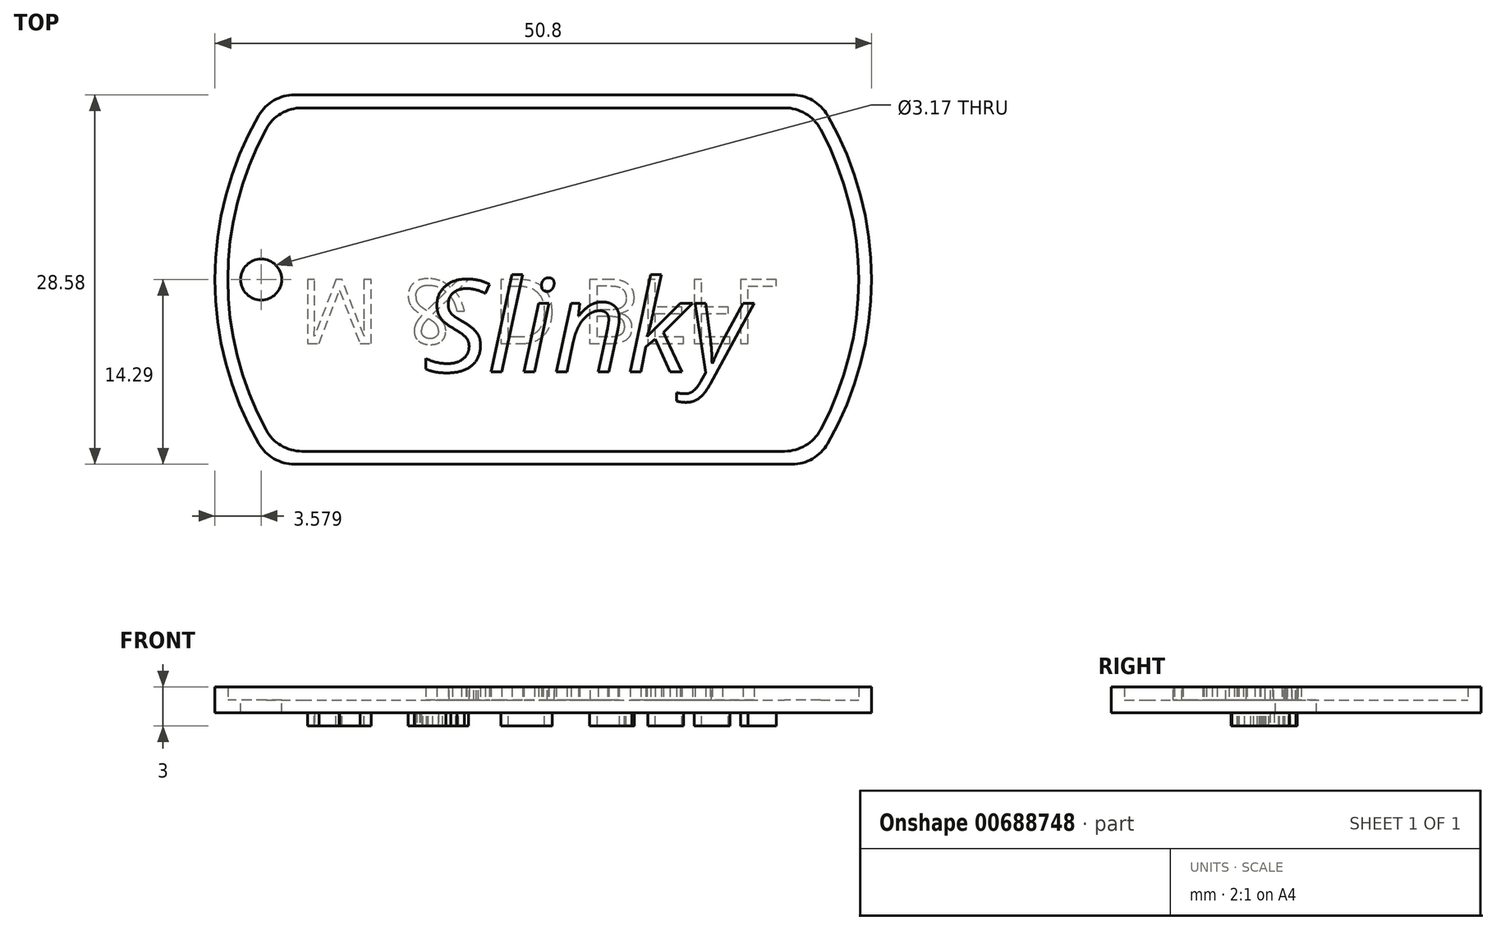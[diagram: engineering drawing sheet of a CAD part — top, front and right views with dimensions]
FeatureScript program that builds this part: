
annotation { "Feature Type Name" : "Feature", "Feature Type Description" : "" }
export const myFeature = defineFeature(function(context is Context, id is Id, definition is map)
    precondition{}
    {
        {
            var Q0;
            Q0=qCreatedBy(makeId("Top.planeOp"),FACE);
            var sketch = newSketch(context, id + "F0", { "sketchPlane" : qUnion([Q0])});
            skArc(sketch, "E0", {"start": v(-22, 12.7) * mm, "mid": v(-25.4, 0) * mm, "end": v(-22, -12.7) * mm});
            skLineSegment(sketch, "E1.top", {"start": v(-19.25, -14.29) * mm, "end": v(19.25, -14.29) * mm});
            skArc(sketch, "E2.trimOffspring", {"start": v(22, -12.7) * mm, "mid": v(25.4, 0) * mm, "end": v(22, 12.7) * mm});
            skLineSegment(sketch, "E3", {"start": v(-19.25, 14.29) * mm, "end": v(19.25, 14.29) * mm});
            skPoint(sketch, "E4.visualSharp", {"position": v(-21, 14.29) * mm});
            skArc(sketch, "E4.filletArc", {"start": v(-19.25, 14.29) * mm, "mid": v(-20.83, 13.86) * mm, "end": v(-22, 12.7) * mm});
            skPoint(sketch, "E5.visualSharp", {"position": v(21, 14.29) * mm});
            skArc(sketch, "E5.filletArc", {"start": v(22, 12.7) * mm, "mid": v(20.83, 13.86) * mm, "end": v(19.25, 14.29) * mm});
            skPoint(sketch, "E6.visualSharp", {"position": v(21, -14.29) * mm});
            skArc(sketch, "E6.filletArc", {"start": v(19.25, -14.29) * mm, "mid": v(20.83, -13.86) * mm, "end": v(22, -12.7) * mm});
            skPoint(sketch, "E7.visualSharp", {"position": v(-21, -14.29) * mm});
            skArc(sketch, "E7.filletArc", {"start": v(-22, -12.7) * mm, "mid": v(-20.83, -13.86) * mm, "end": v(-19.25, -14.29) * mm});
            skSolve(sketch);
        }
        {
            var Q0;
            Q0=makeQuery(id+"F0.imprint","IMPRINT",FACE,{"disambiguationData":[TD([[makeQuery(id+"F0.imprint","IMPRINT",EDGE,{"derivedFrom":sQuery(id+"F0.wireOp",EDGE,"E0")}),1.0]])]});
            extrude(context, id + "F1", {"entities" : qUnion([Q0]), "depth" : 1 * mm, "offsetDistance" : 25.4 * mm});
        }
        {
            var Q0;
            Q0=makeQuery(id+"F1.opExtrude","CAP_FACE",FACE,{"disambiguationData":[OSD([sQuery(id+"F0.wireOp",EDGE,"E0"),sQuery(id+"F0.wireOp",EDGE,"E1.top"),sQuery(id+"F0.wireOp",EDGE,"E2.trimOffspring"),sQuery(id+"F0.wireOp",EDGE,"E3"),sQuery(id+"F0.wireOp",EDGE,"E4.filletArc"),sQuery(id+"F0.wireOp",EDGE,"E5.filletArc"),sQuery(id+"F0.wireOp",EDGE,"E6.filletArc"),sQuery(id+"F0.wireOp",EDGE,"E7.filletArc")])],"isStart":false});
            var sketch = newSketch(context, id + "F2", { "sketchPlane" : qUnion([Q0])});
            skLineSegment(sketch, "E8.0", {"start": v(-18.66, 13.29) * mm, "end": v(18.66, 13.29) * mm});
            skArc(sketch, "E8.1", {"start": v(-21.45, 11.63) * mm, "mid": v(-24.4, 0) * mm, "end": v(-21.45, -11.63) * mm});
            skLineSegment(sketch, "E8.2", {"start": v(-18.66, -13.29) * mm, "end": v(18.66, -13.29) * mm});
            skArc(sketch, "E8.3", {"start": v(21.45, -11.63) * mm, "mid": v(24.4, 0) * mm, "end": v(21.45, 11.63) * mm});
            skPoint(sketch, "E9.visualSharp", {"position": v(-20.46, 13.29) * mm});
            skArc(sketch, "E9.filletArc", {"start": v(-18.66, 13.29) * mm, "mid": v(-20.29, 12.84) * mm, "end": v(-21.45, 11.63) * mm});
            skPoint(sketch, "E10.visualSharp", {"position": v(20.46, 13.29) * mm});
            skArc(sketch, "E10.filletArc", {"start": v(21.45, 11.63) * mm, "mid": v(20.29, 12.84) * mm, "end": v(18.66, 13.29) * mm});
            skPoint(sketch, "E11.visualSharp", {"position": v(20.46, -13.29) * mm});
            skArc(sketch, "E11.filletArc", {"start": v(18.66, -13.29) * mm, "mid": v(20.29, -12.84) * mm, "end": v(21.45, -11.63) * mm});
            skPoint(sketch, "E12.visualSharp", {"position": v(-20.46, -13.29) * mm});
            skArc(sketch, "E12.filletArc", {"start": v(-21.45, -11.63) * mm, "mid": v(-20.29, -12.84) * mm, "end": v(-18.66, -13.29) * mm});
            skLineSegment(sketch, "E13.0", {"start": v(-19.25, 14.29) * mm, "end": v(19.25, 14.29) * mm});
            skArc(sketch, "E13.1", {"start": v(-22, 12.7) * mm, "mid": v(-25.4, 0) * mm, "end": v(-22, -12.7) * mm});
            skLineSegment(sketch, "E13.2", {"start": v(-19.25, -14.29) * mm, "end": v(19.25, -14.29) * mm});
            skArc(sketch, "E13.3", {"start": v(22, -12.7) * mm, "mid": v(25.4, 0) * mm, "end": v(22, 12.7) * mm});
            skPoint(sketch, "E14.visualSharp", {"position": v(-21, -14.29) * mm});
            skArc(sketch, "E14.filletArc", {"start": v(-22, -12.7) * mm, "mid": v(-20.83, -13.86) * mm, "end": v(-19.25, -14.29) * mm});
            skPoint(sketch, "E15.visualSharp", {"position": v(21, -14.29) * mm});
            skArc(sketch, "E15.filletArc", {"start": v(19.25, -14.29) * mm, "mid": v(20.83, -13.86) * mm, "end": v(22, -12.7) * mm});
            skPoint(sketch, "E16.visualSharp", {"position": v(21, 14.29) * mm});
            skArc(sketch, "E16.filletArc", {"start": v(22, 12.7) * mm, "mid": v(20.83, 13.86) * mm, "end": v(19.25, 14.29) * mm});
            skPoint(sketch, "E17.visualSharp", {"position": v(-21, 14.29) * mm});
            skArc(sketch, "E17.filletArc", {"start": v(-19.25, 14.29) * mm, "mid": v(-20.83, 13.86) * mm, "end": v(-22, 12.7) * mm});
            skSolve(sketch);
        }
        {
            var Q0;
            Q0=makeQuery(id+"F2.imprint","IMPRINT",FACE,{"disambiguationData":[TD([[makeQuery(id+"F2.imprint","IMPRINT",EDGE,{"derivedFrom":sQuery(id+"F2.wireOp",EDGE,"E8.0")}),1.0]])]});
            extrude(context, id + "F3", {"entities" : qUnion([Q0]), "operationType" : NewBodyOperationType.ADD, "depth" : 1 * mm, "offsetDistance" : 25.4 * mm});
        }
        {
            var Q0;
            Q0=makeQuery(id+"F1.opExtrude","CAP_FACE",FACE,{"disambiguationData":[OSD([sQuery(id+"F0.wireOp",EDGE,"E0"),sQuery(id+"F0.wireOp",EDGE,"E1.top"),sQuery(id+"F0.wireOp",EDGE,"E2.trimOffspring"),sQuery(id+"F0.wireOp",EDGE,"E3"),sQuery(id+"F0.wireOp",EDGE,"E4.filletArc"),sQuery(id+"F0.wireOp",EDGE,"E5.filletArc"),sQuery(id+"F0.wireOp",EDGE,"E6.filletArc"),sQuery(id+"F0.wireOp",EDGE,"E7.filletArc")])],"isStart":false});
            var sketch = newSketch(context, id + "F4", { "sketchPlane" : qUnion([Q0])});
            skCircle(sketch, "E18", {"center": v(-21.82, 0) * mm, "radius": 1.59 * mm});
            skSolve(sketch);
        }
        {
            var Q0;
            Q0=makeQuery(id+"F4.imprint","IMPRINT",FACE,{"disambiguationData":[TD([[makeQuery(id+"F4.imprint","IMPRINT",EDGE,{"derivedFrom":sQuery(id+"F4.wireOp",EDGE,"E18")}),1.0]])]});
            extrude(context, id + "F5", {"entities" : qUnion([Q0]), "operationType" : NewBodyOperationType.REMOVE, "oppositeDirection" : true, "depth" : 1 * mm, "offsetDistance" : 25.4 * mm});
        }
        {
            var Q0;
            Q0=makeQuery(id+"F1.opExtrude","CAP_FACE",FACE,{"disambiguationData":[OSD([sQuery(id+"F0.wireOp",EDGE,"E0"),sQuery(id+"F0.wireOp",EDGE,"E1.top"),sQuery(id+"F0.wireOp",EDGE,"E2.trimOffspring"),sQuery(id+"F0.wireOp",EDGE,"E3"),sQuery(id+"F0.wireOp",EDGE,"E4.filletArc"),sQuery(id+"F0.wireOp",EDGE,"E5.filletArc"),sQuery(id+"F0.wireOp",EDGE,"E6.filletArc"),sQuery(id+"F0.wireOp",EDGE,"E7.filletArc")])],"isStart":false});
            var sketch = newSketch(context, id + "F6", { "sketchPlane" : qUnion([Q0])});
            skText(sketch, "E19", { "text": "Drew", "fontName": "OpenSans-Italic.ttf"});
            const initialGuessF6  = {"E19": [-0.00639, -0.005, 1, 0, 0.005]};
            skSetInitialGuess(sketch, initialGuessF6);
            skSolve(sketch);
        }
        {
            var Q0;
            Q0=makeQuery(id+"F6.imprint","IMPRINT",FACE,{"disambiguationData":[TD([[makeQuery(id+"F6.imprint","IMPRINT",EDGE,{"derivedFrom":sQuery(id+"F6.wireOp",EDGE,"E19.sketch_text.stroke-0")}),1.0]])]});
            var sketch = newSketch(context, id + "F7", { "sketchPlane" : qUnion([Q0])});
            skText(sketch, "E20", { "text": "Adams", "fontName": "OpenSans-Italic.ttf"});
            const initialGuessF7  = {"E20": [-0.00664, -0.01277, 1, 0, 0.005]};
            skSetInitialGuess(sketch, initialGuessF7);
            skSolve(sketch);
        }
        {
            var Q0;
            Q0=makeQuery(id+"F1.opExtrude","CAP_FACE",FACE,{"disambiguationData":[OSD([sQuery(id+"F0.wireOp",EDGE,"E0"),sQuery(id+"F0.wireOp",EDGE,"E1.top"),sQuery(id+"F0.wireOp",EDGE,"E2.trimOffspring"),sQuery(id+"F0.wireOp",EDGE,"E3"),sQuery(id+"F0.wireOp",EDGE,"E4.filletArc"),sQuery(id+"F0.wireOp",EDGE,"E5.filletArc"),sQuery(id+"F0.wireOp",EDGE,"E6.filletArc"),sQuery(id+"F0.wireOp",EDGE,"E7.filletArc")])],"isStart":true});
            var sketch = newSketch(context, id + "F8", { "sketchPlane" : qUnion([Q0])});
            skText(sketch, "E21", { "text": "M & D BFFL", "fontName": "OpenSans-Regular.ttf"});
            const initialGuessF8  = {"E21": [-0.0189, 0, 1, 0, 0.005]};
            skSetInitialGuess(sketch, initialGuessF8);
            skSolve(sketch);
        }
        {
            var Q0;
            Q0 = qSketchRegion(id + "F8", true);
            var Q1;
            Q1 = qSketchRegion(id + "F7", true);
            var Q2;
            Q2 = qSketchRegion(id + "F6", true);
            extrude(context, id + "F9", {"entities" : qUnion([Q0, Q1, Q2]), "operationType" : NewBodyOperationType.ADD, "depth" : 1 * mm, "offsetDistance" : 25.4 * mm});
        }
        {
            var Q0;
            Q0=makeQuery(id+"F1.opExtrude","CAP_FACE",FACE,{"disambiguationData":[OSD([sQuery(id+"F0.wireOp",EDGE,"E0"),sQuery(id+"F0.wireOp",EDGE,"E1.top"),sQuery(id+"F0.wireOp",EDGE,"E2.trimOffspring"),sQuery(id+"F0.wireOp",EDGE,"E3"),sQuery(id+"F0.wireOp",EDGE,"E4.filletArc"),sQuery(id+"F0.wireOp",EDGE,"E5.filletArc"),sQuery(id+"F0.wireOp",EDGE,"E6.filletArc"),sQuery(id+"F0.wireOp",EDGE,"E7.filletArc")])],"isStart":false});
            var sketch = newSketch(context, id + "F10", { "sketchPlane" : qUnion([Q0])});
            skText(sketch, "E22", { "text": "Slinky ", "fontName": "OpenSans-Italic.ttf"});
            const initialGuessF10  = {"E22": [-0.00927, -0.00713, 1, 0, 0.00713]};
            skSetInitialGuess(sketch, initialGuessF10);
            skSolve(sketch);
        }
        {
            var Q0;
            Q0 = qSketchRegion(id + "F10", true);
            extrude(context, id + "F11", {"entities" : qUnion([Q0]), "operationType" : NewBodyOperationType.ADD, "depth" : 1 * mm, "offsetDistance" : 25.4 * mm});
        }
    });
